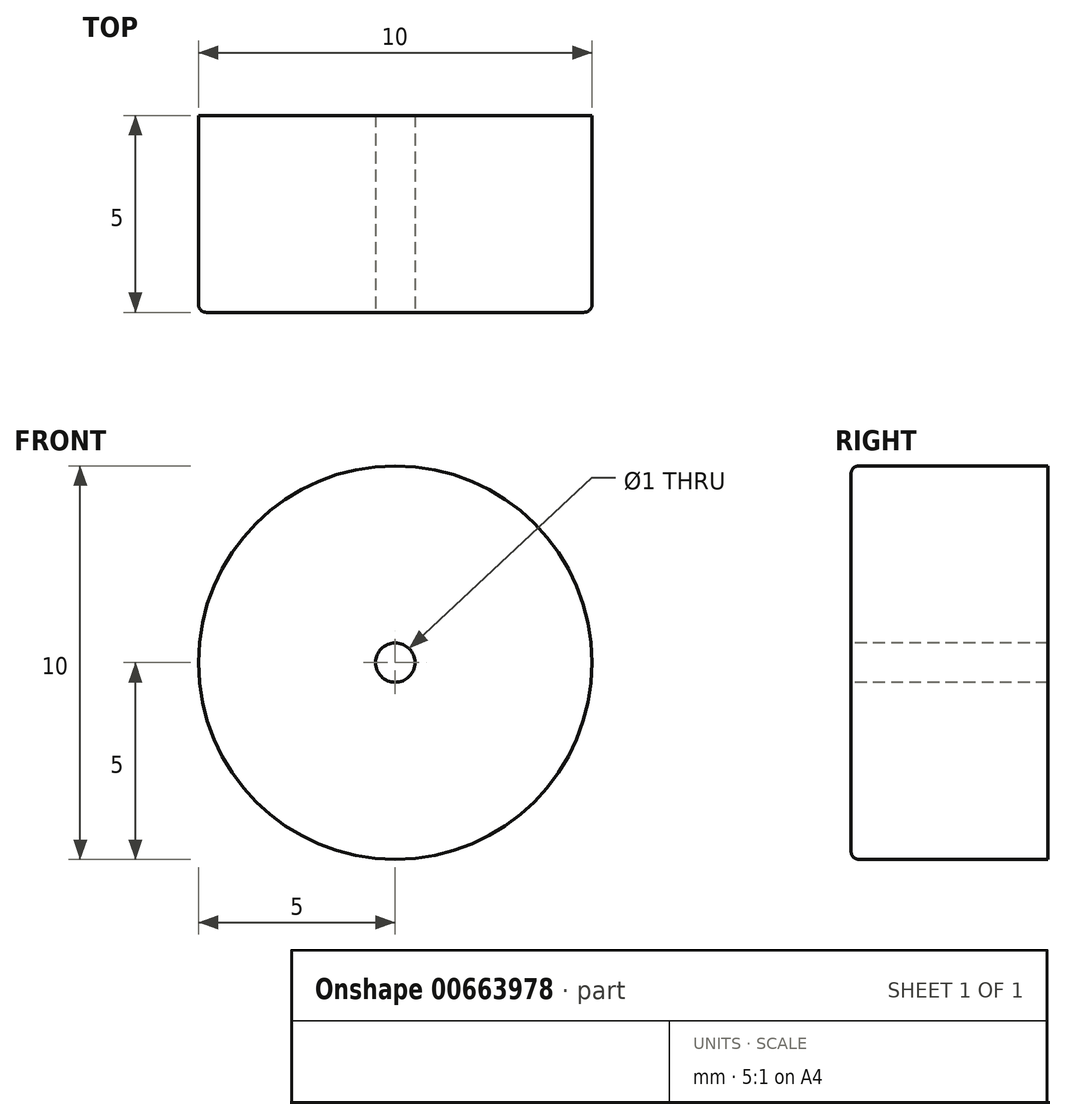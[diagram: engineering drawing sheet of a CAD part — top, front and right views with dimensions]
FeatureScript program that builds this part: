
annotation { "Feature Type Name" : "Feature", "Feature Type Description" : "" }
export const myFeature = defineFeature(function(context is Context, id is Id, definition is map)
    precondition{}
    {
        {
            var Q0;
            Q0=qCreatedBy(makeId("Front.planeOp"),FACE);
            var sketch = newSketch(context, id + "F0", { "sketchPlane" : qUnion([Q0])});
            skCircle(sketch, "E0", {"center": v(0, 0) * mm, "radius": 5 * mm});
            skSolve(sketch);
        }
        {
            var Q0;
            Q0 = qSketchRegion(id + "F0", true);
            extrude(context, id + "F1", {"entities" : qUnion([Q0]), "depth" : 5 * mm, "offsetDistance" : 25 * mm});
        }
        {
            var Q0;
            Q0=makeQuery(id+"F1.opExtrude","CAP_FACE",FACE,{"disambiguationData":[OSD([sQuery(id+"F0.wireOp",EDGE,"E0")])],"isStart":false});
            var sketch = newSketch(context, id + "F2", { "sketchPlane" : qUnion([Q0])});
            skCircle(sketch, "E1", {"center": v(0, 0) * mm, "radius": 0.5 * mm});
            skSolve(sketch);
        }
        {
            var Q0;
            Q0 = qSketchRegion(id + "F2", true);
            extrude(context, id + "F3", {"entities" : qUnion([Q0]), "operationType" : NewBodyOperationType.REMOVE, "oppositeDirection" : true, "depth" : 6 * mm, "offsetDistance" : 25 * mm});
        }
        {
            var Q0;
            Q0=makeQuery(id+"F1.opExtrude","CAP_EDGE",EDGE,{"disambiguationData":[OSD([sQuery(id+"F0.wireOp",EDGE,"E0")])],"isStart":false});
            fillet(context, id + "F4", {"entities" : qUnion([Q0]), "radius" : .2 * mm, "tangentPropagation" : true, "allowEdgeOverflow" : false});
        }
    });
